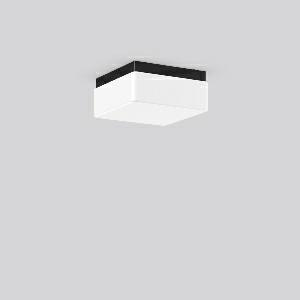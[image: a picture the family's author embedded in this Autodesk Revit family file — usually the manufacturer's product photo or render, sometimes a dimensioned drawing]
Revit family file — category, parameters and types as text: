
# Revit family: quadrat_20128_003_8e59
name_source: partatom
category: Lighting Fixtures
units: mm (PartAtom-declared; Revit-internal decimal feet)

## family parameters
Cut with Voids When Loaded = No
Host = Face
Light Source = No
Part Type = Normal
Room Calculation Point = No
Round Connector Dimension = Use Diameter
Shared = No

## types (1)
- QUADRAT (1 x QA60/clear E27, 915 lm, 57 W, 3000)
    Apparent Load = 57 VA
    CIE Flux Codes = 34 63 85 72 42
    Color Rendering = 90
    Color Temperature = 3000
    Default Elevation = 1800 mm
    Description = Series: QUADRAT
Square surface-mounted luminaire in classic design. Base: plastic. Opal glass: mouth blown, silk finish. Diffuser fastening: spring system. Suitable for Ceiling mounting, Wall (surface). IP 43 ceiling mounting, IP 44 wall mounting. 
Colour: black
Length: 240 mm
Width: 240 mm
Height: 110 mm
Lamp: A60
Number of lamps: 1
Wattage: 75 W
Socket: E27
System power: 60 W
Rated luminous flux: 310 lm
Luminous efficiency: 5 lm/W
Control gear: Converter not necessary
Protection class: II
Type of protection: IP 43
    Height = 110 mm
    Lamp = 1 x QA60/clear E27
    Lamp Light Flux = 915 lm
    Lamp Power = 57 W
    Lamp count = 1
    Length = 240 mm
    Lifetime = 3000 h
    Luminous efficacy = 7 lm/W
    Manufacturer = RZB
    ModVariant = No
    Model = 20128.003
    Mounting Place = Ceiling
    Mounting Type = Surface mounted
    Number of Poles = 1
    OnlyDefault = Yes
    Power Factor = 1
    Product Name = QUADRAT
    Product group = Surface mounted ceiling and wall luminaires
    ProductGroupID = 305
    Protection Class = Protection class II
    Protection Degree = IP 43
    RLX_Detail_Level = 1
    RLX_Emergency_Light_Flux = 0 lm
    RLX_Emergency_Type = 0
    RLX_Emergency_Type_DB = No
    RlxData = <blob elided: 11613 chars, md5=20a36b7a>
    Socket = E27
    Standby Power = 0 W
    System Light Flux = 387 lm
    System Power = 57 W
    Type Comments = Product without accessories
    Type Image = 20128.003.jpg
    URL = http://relux.com
    VarID = ---
    Voltage = 0 V
    Weight = 0.00 kg
    Width = 240 mm

## geometry (parser evidence)
native form markers: Sweep x12
no freeform markers — native parametric forms only
